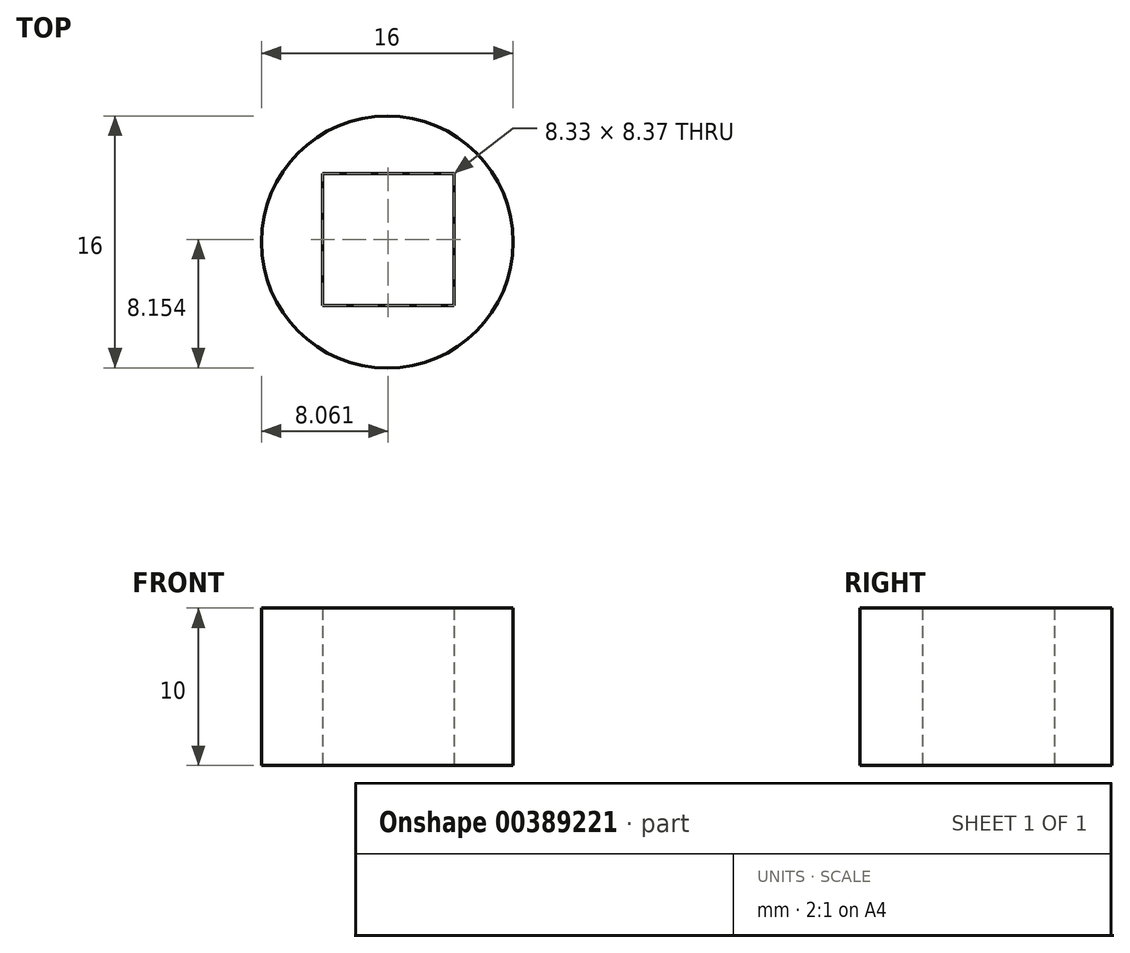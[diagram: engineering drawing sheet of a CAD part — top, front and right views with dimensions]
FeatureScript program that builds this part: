
annotation { "Feature Type Name" : "Feature", "Feature Type Description" : "" }
export const myFeature = defineFeature(function(context is Context, id is Id, definition is map)
    precondition{}
    {
        {
            var Q0;
            Q0=qCreatedBy(makeId("Top.planeOp"),FACE);
            var sketch = newSketch(context, id + "F0", { "sketchPlane" : qUnion([Q0])});
            skCircle(sketch, "E0", {"center": v(-41.3, 22.47) * mm, "radius": 8 * mm});
            skLineSegment(sketch, "E1", {"start": v(-48.22, 18.44) * mm, "end": v(-34.4, 18.44) * mm});
            skLineSegment(sketch, "E2", {"start": v(-34.59, 26.8) * mm, "end": v(-48.03, 26.8) * mm});
            skLineSegment(sketch, "E3", {"start": v(-37.08, 26.8) * mm, "end": v(-37.08, 18.44) * mm});
            skLineSegment(sketch, "E4", {"start": v(-45.41, 26.8) * mm, "end": v(-45.41, 18.44) * mm});
            skPoint(sketch, "E5.orphan", {"position": v(-41.3, 34.06) * mm});
            skPoint(sketch, "E6.start.orphan", {"position": v(-52.66, 22.47) * mm});
            skSolve(sketch);
        }
        {
            var Q0;
            Q0 = qSketchRegion(id + "F0", true);
            extrude(context, id + "F1", {"entities" : qUnion([Q0]), "depth" : 10 * mm});
        }
    });
